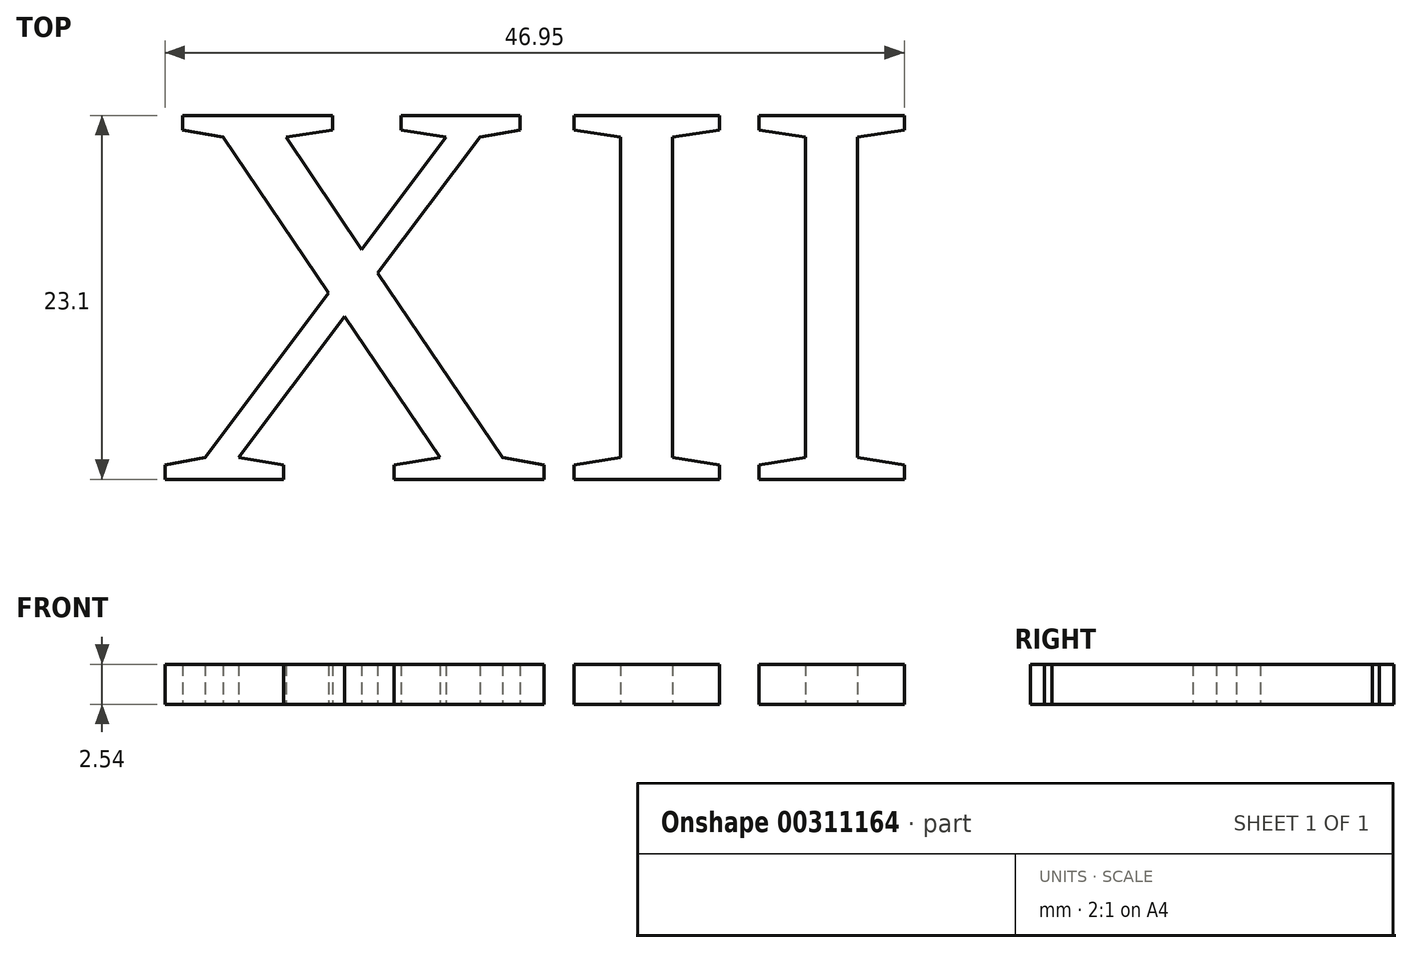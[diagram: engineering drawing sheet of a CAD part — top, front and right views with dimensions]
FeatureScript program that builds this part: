
annotation { "Feature Type Name" : "Feature", "Feature Type Description" : "" }
export const myFeature = defineFeature(function(context is Context, id is Id, definition is map)
    precondition{}
    {
        {
            var Q0;
            Q0=qCreatedBy(makeId("Top.planeOp"),FACE);
            var sketch = newSketch(context, id + "F0", { "sketchPlane" : qUnion([Q0])});
            skText(sketch, "E0", { "text": "XII", "fontName": "Tinos-Regular.ttf"});
            const initialGuessF0  = {"E0": [0.00043, 0.00065, 1, 0, 0.0254]};
            skSetInitialGuess(sketch, initialGuessF0);
            skSolve(sketch);
        }
        {
            var Q0;
            Q0 = qSketchRegion(id + "F0", true);
            extrude(context, id + "F1", {"entities" : qUnion([Q0]), "depth" : 2.54 * mm});
        }
    });
